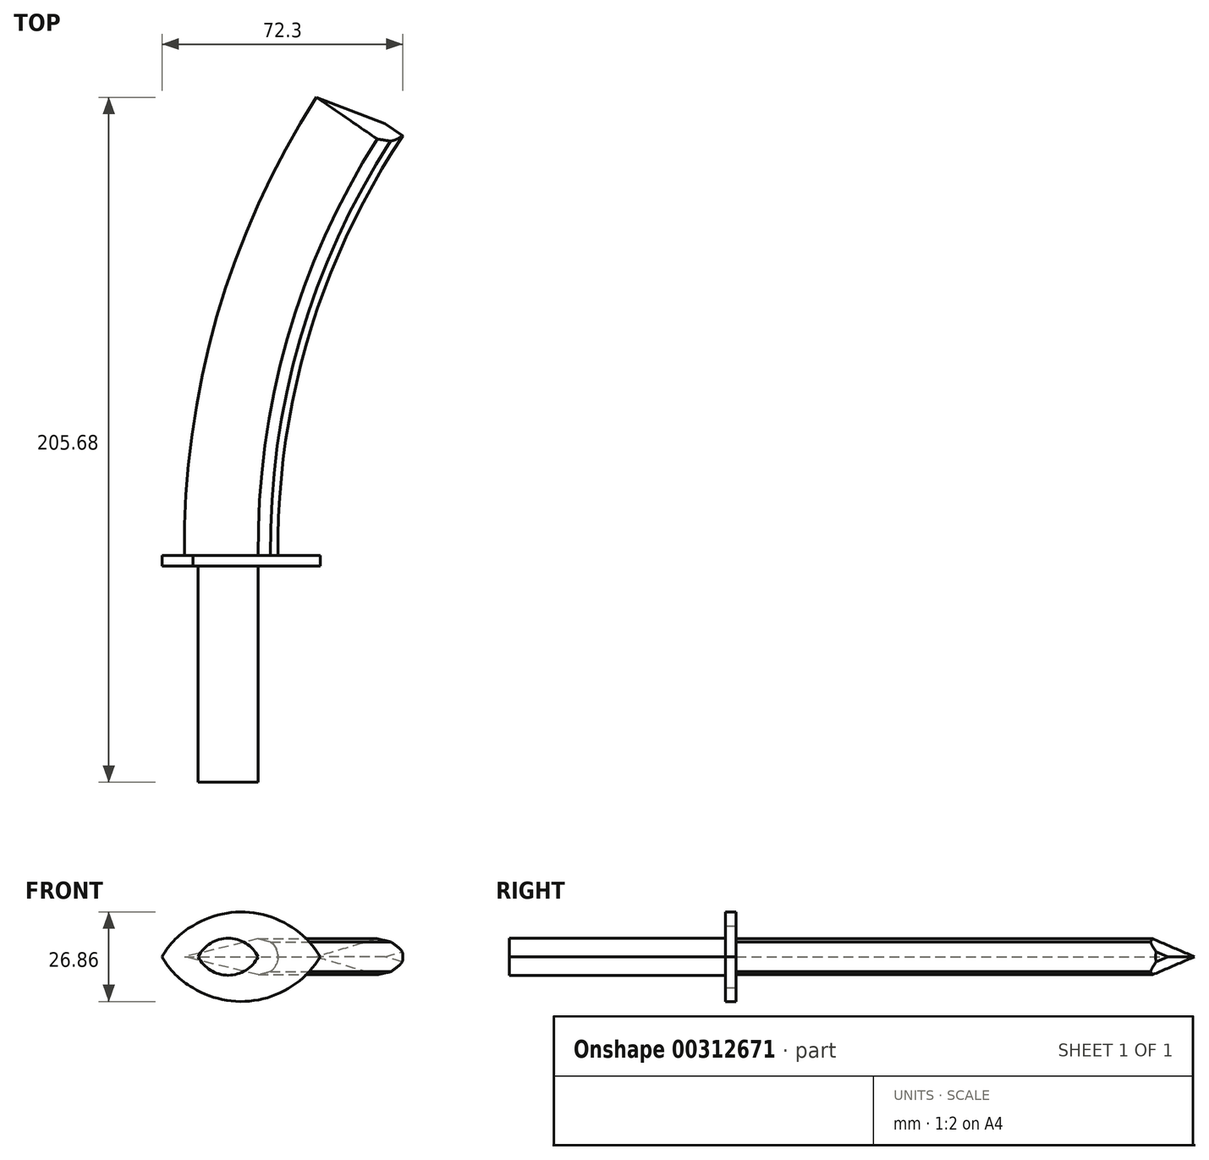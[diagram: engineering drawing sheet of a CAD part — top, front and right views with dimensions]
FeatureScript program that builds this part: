
annotation { "Feature Type Name" : "Feature", "Feature Type Description" : "" }
export const myFeature = defineFeature(function(context is Context, id is Id, definition is map)
    precondition{}
    {
        {
            var Q0;
            Q0=qCreatedBy(makeId("Front.planeOp"),FACE);
            var sketch = newSketch(context, id + "F0", { "sketchPlane" : qUnion([Q0])});
            skLineSegment(sketch, "E0", {"start": v(0, 5.4) * mm, "end": v(-22.15, 0) * mm});
            skLineSegment(sketch, "E1.MirrorCS", {"start": v(0, 5.4) * mm, "end": v(3.71, 4.49) * mm});
            skPoint(sketch, "E2.end.orphan", {"position": v(-34.69, 0) * mm});
            skPoint(sketch, "E3.MirrorCS.end.orphan", {"position": v(34.69, 0) * mm});
            skPoint(sketch, "E3.MirrorCS.start.orphan", {"position": v(0, 5.4) * mm});
            skLineSegment(sketch, "E4.MirrorCS", {"start": v(0, -5.4) * mm, "end": v(3.66, -4.5) * mm});
            skLineSegment(sketch, "E5.MirrorCS", {"start": v(0, -5.4) * mm, "end": v(-22.15, 0) * mm});
            skArc(sketch, "E6", {"start": v(18.64, 0) * mm, "mid": v(1.44, 12.64) * mm, "end": v(-19.64, 9.3) * mm});
            skArc(sketch, "E7.trimOffspring", {"start": v(-19.64, 9.3) * mm, "mid": v(-24.9, 5.3) * mm, "end": v(-28.84, 0) * mm});
            skPoint(sketch, "E8.orphan", {"position": v(-28.84, 0) * mm});
            skPoint(sketch, "E9.MirrorCS.start.orphan", {"position": v(12.68, 0) * mm});
            skArc(sketch, "E10.MirrorCS", {"start": v(18.64, 0) * mm, "mid": v(1.44, -12.64) * mm, "end": v(-19.64, -9.3) * mm});
            skArc(sketch, "E11.MirrorCS", {"start": v(-19.64, -9.3) * mm, "mid": v(-24.9, -5.3) * mm, "end": v(-28.84, 0) * mm});
            skArc(sketch, "E12", {"start": v(3.66, -4.5) * mm, "mid": v(5.96, -0.02) * mm, "end": v(3.71, 4.49) * mm});
            skPoint(sketch, "E13.trimOffspring.end.orphan", {"position": v(22.15, 0) * mm});
            skSolve(sketch);
        }
        {
            var Q0;
            Q0=qCreatedBy(makeId("Top.planeOp"),FACE);
            var sketch = newSketch(context, id + "F1", { "sketchPlane" : qUnion([Q0])});
            skArc(sketch, "E14", {"start": v(38.55, 129.35) * mm, "mid": v(9.47, 67.6) * mm, "end": v(0, 0) * mm});
            skSolve(sketch);
        }
        {
            var Q0;
            Q0=makeQuery(id+"F0.imprint","IMPRINT",FACE,{"disambiguationData":[TD([[makeQuery(id+"F0.imprint","IMPRINT",EDGE,{"derivedFrom":sQuery(id+"F0.wireOp",EDGE,"E0")}),1.0]])]});
            var Q1;
            Q1=sQuery(id+"F1.wireOp",EDGE,"E14");
            sweep(context, id + "F2", {"profiles" : qUnion([Q0]), "path" : qUnion([Q1])});
        }
        {
            var Q0;
            {var subQ5=sQuery(id+"F0.wireOp",EDGE,"E0");Q0=makeQuery(id+"F0.imprint","IMPRINT",FACE,{"disambiguationData":[TD([[makeQuery(id+"F0.imprint","IMPRINT",EDGE,{"derivedFrom":subQ5}),-1.0]])]});}
            var Q1;
            {var subQ5=sQuery(id+"F0.wireOp",EDGE,"E0");Q1=makeQuery(id+"F0.imprint","IMPRINT",FACE,{"disambiguationData":[TD([[makeQuery(id+"F0.imprint","IMPRINT",EDGE,{"derivedFrom":subQ5}),1.0]])]});}
            extrude(context, id + "F3", {"entities" : qUnion([Q0, Q1]), "operationType" : NewBodyOperationType.ADD, "depth" : 3.17 * mm});
        }
        {
            var Q0;
            Q0=makeQuery(id+"F2.opSweep","CAP_EDGE",EDGE,{"disambiguationData":[OSD([sQuery(id+"F0.wireOp",EDGE,"E5.MirrorCS"),sQuery(id+"F1.wireOp",VERTEX,"E14.start")])],"isStart":false});
            var Q1;
            Q1=makeQuery(id+"F2.opSweep","CAP_EDGE",EDGE,{"disambiguationData":[OSD([sQuery(id+"F0.wireOp",EDGE,"E0"),sQuery(id+"F1.wireOp",VERTEX,"E14.start")])],"isStart":false});
            chamfer(context, id + "F4", {"entities" : qUnion([Q0, Q1]), "width" : 5.08 * mm, "tangentPropagation" : true});
        }
        {
            var Q0;
            Q0=qCreatedBy(makeId("Front.planeOp"),FACE);
            var sketch = newSketch(context, id + "F5", { "sketchPlane" : qUnion([Q0])});
            skArc(sketch, "E15", {"start": v(0, 0) * mm, "mid": v(-9, 5.56) * mm, "end": v(-18, 0) * mm});
            skArc(sketch, "E16.MirrorCS", {"start": v(0, 0) * mm, "mid": v(-9, -5.56) * mm, "end": v(-18, 0) * mm});
            skSolve(sketch);
        }
        {
            var Q0;
            Q0 = qSketchRegion(id + "F5", true);
            extrude(context, id + "F6", {"entities" : qUnion([Q0]), "operationType" : NewBodyOperationType.ADD, "depth" : 68.07 * mm});
        }
    });
